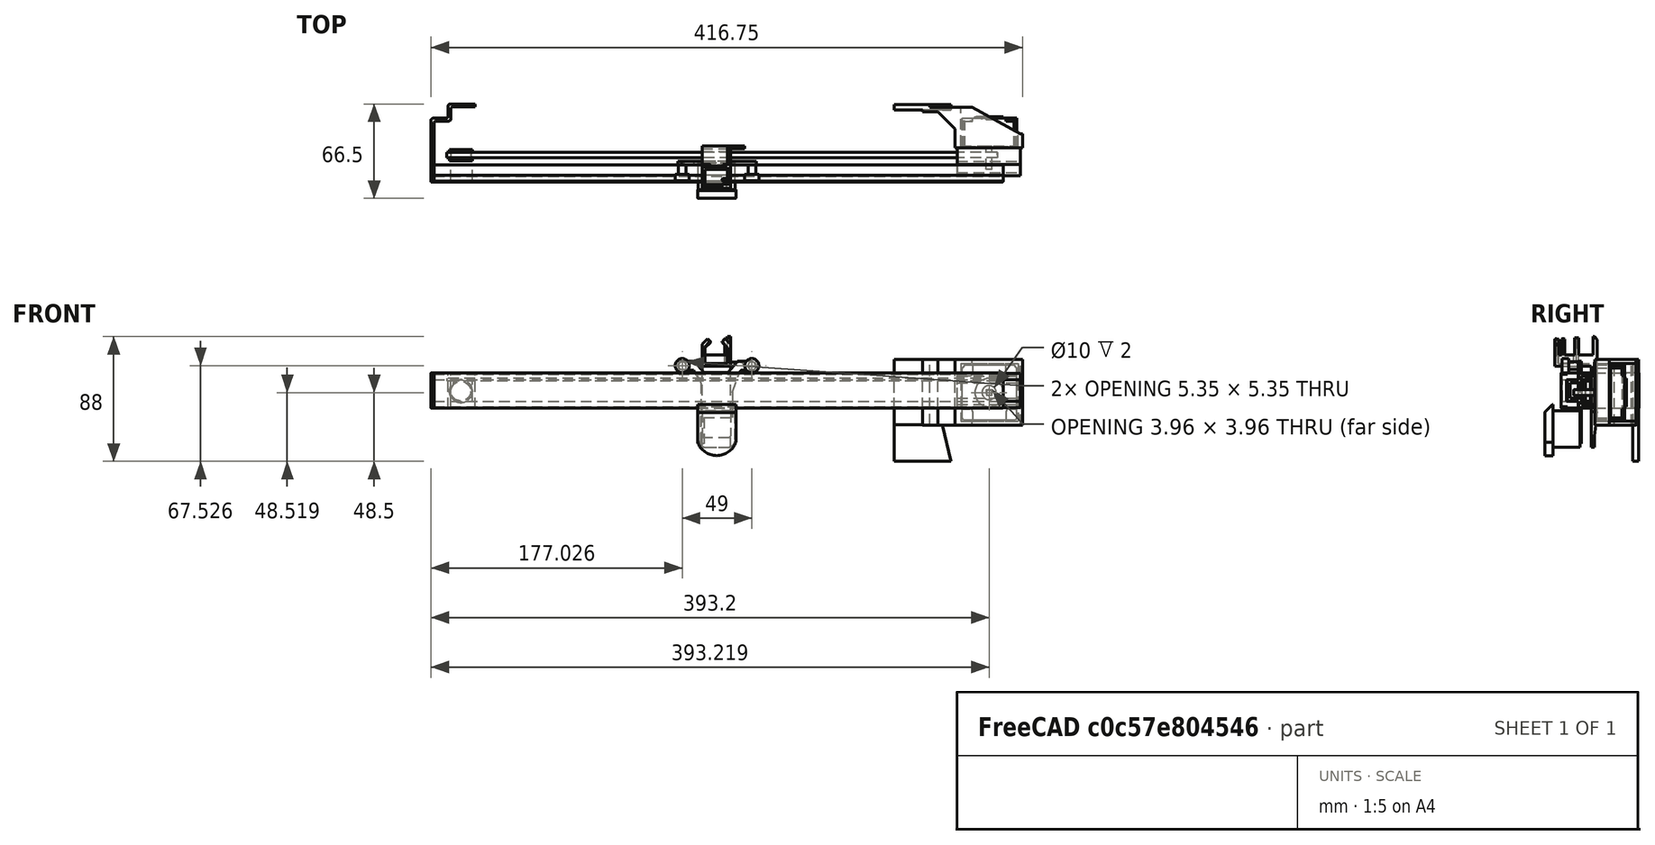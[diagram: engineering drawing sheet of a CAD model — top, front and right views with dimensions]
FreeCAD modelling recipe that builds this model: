
FCSTD DOCUMENT  (FreeCAD 0.15R4671 (Git))
Label: Plotter_Eje_X
License: All rights reserved
LicenseURL: http://en.wikipedia.org/wiki/All_rights_reserved
objects: Part::Box×25, Part::Cut×19, Part::MultiFuse×10, Part::Cylinder×8, Part::Fillet×8, Part::Mirroring×4, Part::Chamfer×3, Part::Fuse×2, Part::Torus×1, App::DocumentObjectGroup×1
note: 80 computed .brp shape members not serialized (recipe doc carries the construction recipe); baked Part::Feature solids carry a one-line shape summary decoded from their .brp

FEATURE [Part::Box] Box  label="chapa no motor 1"
  Height = 25
  Length = 2
  Placement = pos=(-2,0,0) rot=(0,0,1;0rad)
  Width = 45
FEATURE [Part::Box] Box001  label="chapa no motor 2"
  Height = 25
  Length = 2
  Placement = pos=(-1,45,0) rot=(0,0,-1;1.5708rad)
  Width = 13
FEATURE [Part::Box] Box002  label="chapa no motor 003"
  Height = 25
  Length = 2
  Placement = pos=(10,45,0) rot=(0,0,1;0rad)
  Width = 8
FEATURE [Part::Box] Box003  label="chapa no motor 004"
  Height = 25
  Length = 2
  Placement = pos=(10,55,0) rot=(0,0,-1;1.5708rad)
  Width = 19
FEATURE [Part::Fuse] Fusion
  Base = -> Box
  Tool = -> Box001
FEATURE [Part::MultiFuse] Fusion001  label="metal no motor"
  Shapes = -> [Fusion,Box003,Box002]
FEATURE [Part::Torus] Torus  label="Toro"
  Angle1 = -180
  Angle2 = 180
  Angle3 = 360
  Placement = pos=(19,-19,12) rot=(1,0,0;1.5708rad)
  Radius1 = 9
  Radius2 = 2
FEATURE [Part::Cut] Cut  label="polea metal"
  Placement = pos=(0,38,0) rot=(0,0,1;0rad)
  Tool = -> Torus
FEATURE [Part::Box] Box004  label="sujeta polea"
  Height = 15
  Length = 15
  Placement = pos=(12,1,5) rot=(0,0,1;0rad)
  Width = 11
FEATURE [Part::MultiFuse] Fusion002  label="EjeX_Polea no motor"
  Shapes = -> [Cut,Box004]
FEATURE [Part::Cylinder] Cylinder  label="EjeX_correa001"
  Angle = 180
  Height = 388
  Placement = pos=(397,19,21) rot=(-0.57735,-0.57735,0.57735;2.0944rad)
  Radius = 2
FEATURE [Part::Box] Box005  label="Cubo017"
  Height = 1
  Length = 13
  Placement = pos=(49,-10,-33) rot=(0,1,0;0.558505rad)
  Width = 10
FEATURE [Part::Box] Box006  label="Cubo018"
  Height = 3
  Length = 12
  Placement = pos=(49,18,4) rot=(0,0,1;0rad)
  Width = 12
FEATURE [Part::Box] Box007  label="Cubo043"
  Height = 15
  Length = 44.5
  Placement = pos=(414,4,5) rot=(0,0,1;0rad)
  Width = 8
FEATURE [Part::Box] Box008  label="Cubo044"
  Height = 11
  Length = 50.5
  Placement = pos=(412,6,7) rot=(0,0,1;0rad)
  Width = 6
FEATURE [Part::Cut] Cut001
  Base = -> Box007
  Tool = -> Box008
FEATURE [Part::Box] Box009  label="Cubo045"
  Height = 24
  Length = 44.5
  Placement = pos=(414,12,0.5) rot=(0,0,1;0rad)
  Width = 11.5
FEATURE [Part::Box] Box010  label="Cubo046"
  Height = 20
  Length = 44.5
  Placement = pos=(414,14,2.5) rot=(0,0,1;0rad)
  Width = 9.5
FEATURE [Part::Cut] Cut002
  Base = -> Box009
  Tool = -> Box010
FEATURE [Part::Box] Box011  label="Cubo047"
  Height = 11
  Length = 50
  Placement = pos=(412,9,7) rot=(0,0,1;0rad)
  Width = 9
FEATURE [Part::Cut] Cut003
  Base = -> Cut002
  Tool = -> Box011
FEATURE [Part::Fuse] Fusion003  label="V motor"
  Base = -> Cut001
  Placement = pos=(-57.5,0,0) rot=(0,0,1;0rad)
  Tool = -> Cut003
FEATURE [Part::Box] Box012  label="Cubo048"
  Height = 38.5
  Length = 38.5
  Placement = pos=(360,25,-8) rot=(0,0,1;0rad)
  Width = 20
FEATURE [Part::Box] Box013  label="Cubo049"
  Height = 40.5
  Length = 40.5
  Placement = pos=(359,25,-9) rot=(0,0,1;0rad)
  Width = 41
FEATURE [Part::Cut] Cut004
  Tool = -> Box013
FEATURE [Part::Chamfer] Chamfer
  Base = -> Box012
  Edges = 1 edges r=2: [Edge6]
FEATURE [Part::Chamfer] Chamfer001
  Base = -> Chamfer
  Edges = 3 edges: [Edge3 r=1,Edge11 r=1,Edge15 r=2]
FEATURE [Part::Box] Box014  label="Cubo050"
  Height = 7.5
  Length = 7.5
  Placement = pos=(391,43,23) rot=(0,0,1;0rad)
  Width = 3
FEATURE [Part::Box] Box015  label="Cubo051"
  Height = 7.5
  Length = 7.5
  Placement = pos=(391,43,-8) rot=(0,0,1;0rad)
  Width = 3
FEATURE [Part::Box] Box016  label="Cubo052"
  Height = 7.5
  Length = 7.5
  Placement = pos=(360,43,23) rot=(0,0,1;0rad)
  Width = 3
FEATURE [Part::Box] Box017  label="Cubo053"
  Height = 7.5
  Length = 7.5
  Placement = pos=(360,43,-8) rot=(0,0,1;0rad)
  Width = 3
FEATURE [Part::Fillet] Fillet
  Base = -> Box014
  Edges = 1 edges r=2: [Edge4]
FEATURE [Part::Fillet] Fillet001
  Base = -> Box015
  Edges = 1 edges r=2: [Edge2]
FEATURE [Part::Fillet] Fillet002
  Base = -> Box017
  Edges = 1 edges r=2: [Edge6]
FEATURE [Part::Fillet] Fillet003
  Base = -> Box016
  Edges = 1 edges r=2: [Edge8]
FEATURE [Part::Cut] Cut005
  Base = -> Chamfer001
  Tool = -> Fillet
FEATURE [Part::Cut] Cut006
  Base = -> Cut005
  Tool = -> Fillet003
FEATURE [Part::Cut] Cut007
  Base = -> Cut006
  Tool = -> Fillet002
FEATURE [Part::Cut] Cut008  label="motor"
  Base = -> Cut007
  Tool = -> Fillet001
FEATURE [Part::Cylinder] Cylinder001  label="Cilindro012"
  Angle = 360
  Height = 31
  Placement = pos=(379,21,11) rot=(-1,0,0;1.5708rad)
  Radius = 5
FEATURE [Part::Cylinder] Cylinder002  label="Cilindro013"
  Angle = 360
  Height = 11
  Placement = pos=(379,69,11) rot=(-1,0,0;1.5708rad)
  Radius = 10
FEATURE [Part::Cylinder] Cylinder003  label="dentro motor"
  Angle = 360
  Height = 19
  Placement = pos=(379,25,11) rot=(-1,0,0;1.5708rad)
  Radius = 5
FEATURE [Part::Cylinder] Cylinder004  label="Cilindro015"
  Angle = 360
  Height = 31
  Placement = pos=(379,55,11) rot=(-1,0,0;1.5708rad)
  Radius = 5
FEATURE [Part::Cut] Cut009  label="arandeloa motor"
  Base = -> Cylinder002
  Placement = pos=(0,-34,0) rot=(0,0,1;0rad)
  Tool = -> Cylinder004
FEATURE [Part::Cut] Cut010  label="cuerpo motor"
  Base = -> Cut008
  Tool = -> Cylinder001
FEATURE [Part::Box] Box018  label="PARTTE GRANDE"
  Height = 1.8
  Length = 44
  Placement = pos=(0,0,-106) rot=(0,0,1;0rad)
  Width = 43.5
FEATURE [Part::Box] Box019  label="parte alta"
  Height = 1.8
  Length = 15
  Placement = pos=(2,0,-106) rot=(0,-1,0;1.5708rad)
  Width = 43.5
FEATURE [Part::Cylinder] Cylinder005  label="taladro"
  Angle = 360
  Height = 10
  Placement = pos=(-1,3.5,-96.8) rot=(0,1,0;1.5708rad)
  Radius = 2
FEATURE [Part::Mirroring] Part__Mirroring  label="taladro (Mirror #18)"
  Base = (0,0,0)
  Normal = (0,1,0)
  Placement = pos=(0,43.5,0) rot=(0,0,1;0rad)
  Source = -> Cylinder005
FEATURE [Part::Cut] Cut011
  Base = -> Box019
  Tool = -> Cylinder005
FEATURE [Part::Cut] Cut012
  Base = -> Cut011
  Placement = pos=(-0.2,0,0) rot=(0,0,1;0rad)
  Tool = -> Part__Mirroring
FEATURE [Part::Cylinder] Cylinder006  label="tornillos001"
  Angle = 360
  Height = 10
  Placement = pos=(38.5,6.5,-111) rot=(0,0,1;0rad)
  Radius = 1.5
FEATURE [Part::Mirroring] Part__Mirroring001  label="Cilindro020 (Mirror #19)"
  Base = (0,0,0)
  Normal = (1,0,0)
  Placement = pos=(46,0,0) rot=(0,0,1;0rad)
  Source = -> Cylinder006
FEATURE [Part::Mirroring] Part__Mirroring002  label="Cilindro020 (Mirror #20)"
  Base = (0,0,0)
  Normal = (0,1,0)
  Placement = pos=(0,43,0) rot=(0,0,1;0rad)
  Source = -> Part__Mirroring001
FEATURE [Part::Mirroring] Part__Mirroring003  label="Cilindro020 (Mirror #21)"
  Base = (0,0,0)
  Normal = (1,0,0)
  Placement = pos=(46,0,0) rot=(0,0,1;0rad)
  Source = -> Part__Mirroring002
FEATURE [Part::MultiFuse] Fusion004
  Shapes = -> [Cut012,Box018]
FEATURE [Part::Fillet] Fillet004
  Base = -> Fusion004
  Edges = 1 edges r=1.5: [Edge27]
FEATURE [Part::Fillet] Fillet005  label="SUJETA MOTOR PEGADO"
  Base = -> Fillet004
  Edges = 1 edges r=1: [Edge21]
FEATURE [Part::Cut] Cut013
  Base = -> Fillet005
  Tool = -> Cylinder006
FEATURE [Part::Cut] Cut014
  Base = -> Cut013
  Tool = -> Part__Mirroring001
FEATURE [Part::Cut] Cut015
  Base = -> Cut014
  Tool = -> Part__Mirroring002
FEATURE [Part::Cut] Cut016  label="sujeta motor eje Z1"
  Base = -> Cut015
  Placement = pos=(-49,10.2,0) rot=(0,0,1;0rad)
  Tool = -> Part__Mirroring003
FEATURE [Part::Chamfer] Chamfer002  label="SUJETA MOTOR EJE "Z 1""
  Base = -> Cut016
  Edges = 2 edges r=2.5: [Edge6,Edge36]
  Placement = pos=(-58,5,-0.8) rot=(0,0,-1;1.5708rad)
FEATURE [Part::Fillet] Fillet006
  Base = -> Fusion001
  Edges = 6 edges r=1.5: [Edge3,Edge9,Edge11,Edge15,Edge22,Edge27]
FEATURE [Part::Fillet] Fillet007  label="EjeX_Guia_Metal"
  Base = -> Fillet006
  Edges = 2 edges r=1: [Edge6,Edge22]
FEATURE [Part::Box] Box020  label="arreglo"
  Height = 1.8
  Length = 5
  Placement = pos=(-43.8,44,-106.8) rot=(0,0,1;0rad)
  Width = 5
FEATURE [Part::Box] Box021  label="arreglo001"
  Height = 1.8
  Length = 5
  Placement = pos=(-13.8,13,-106.8) rot=(0,0,1;0rad)
  Width = 5
FEATURE [Part::Box] Box022  label="arreglo002"
  Height = 1.8
  Length = 5
  Placement = pos=(-13.8,44,-106.8) rot=(0,0,1;0rad)
  Width = 5
FEATURE [Part::Box] Box023  label="arreglo003"
  Height = 1.8
  Length = 5
  Placement = pos=(-43.8,13,-106.8) rot=(0,0,1;0rad)
  Width = 5
FEATURE [Part::MultiFuse] Fusion005
  Shapes = -> [Box020,Box023,Box021,Box022,Chamfer002]
FEATURE [Part::Box] Box024  label="rebaba003"
  Height = 3
  Length = 505
  Placement = pos=(0,0.6,24) rot=(0,0,1;0rad)
  Width = 4
FEATURE [Part::Cut] Cut017  label="EjeX_guia"
  Tool = -> Box024
FEATURE [Part::Cylinder] Cylinder007  label="eje motor001"
  Angle = 360
  Height = 36
  Placement = pos=(379,9,11) rot=(-1,0,0;1.5708rad)
  Radius = 2
FEATURE [Part::MultiFuse] Fusion007
  Shapes = -> [Cut010,Cut009,Cylinder003]
FEATURE [Part::MultiFuse] Fusion006  label="EjeX_motor"
  Placement = pos=(12.2,0,0) rot=(0,0,1;0rad)
  Shapes = -> [Fusion007,Cylinder007]
FEATURE [Part::MultiFuse] Fusion009  label="sujeta motor004"
  Shapes = -> [Fusion003,Cut004]
FEATURE [Part::MultiFuse] Fusion008  label="EjeX_sujeta motor EJE-X"
  Placement = pos=(12.2,0.5,0) rot=(0,0,1;0rad)
  Shapes = -> [Fusion009]
FEATURE [Part::MultiFuse] Fusion010
  Shapes = -> [Box005,Box006]
FEATURE [Part::MultiFuse] Fusion011
  Shapes = -> [Fusion005,Fillet003,Fusion001,Fillet005]
FEATURE [Part::Cut] Cut018
  Base = -> Fusion011
  Placement = pos=(224,14.5,30) rot=(0,0,1;0rad)
  Tool = -> Fusion010
FEATURE [App::DocumentObjectGroup] Grupo  label="EjeX"
  Group = -> [Fusion006,Fusion008,Cut017,Fillet007,Fusion002,Cylinder,Cut018]
